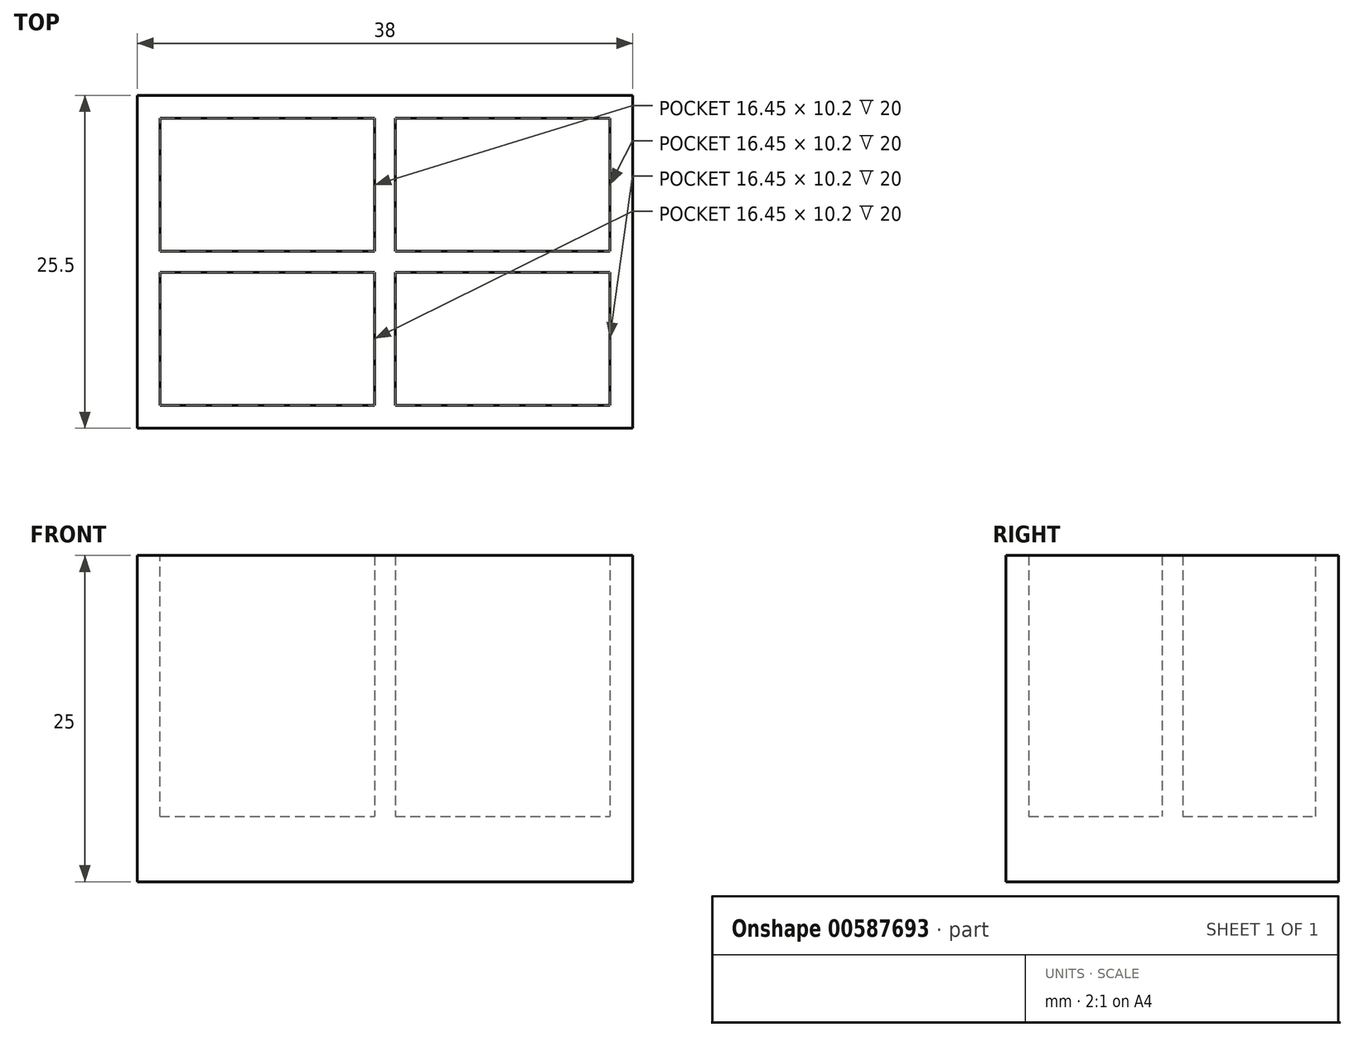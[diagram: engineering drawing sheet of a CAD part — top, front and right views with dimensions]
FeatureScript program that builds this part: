
annotation { "Feature Type Name" : "Feature", "Feature Type Description" : "" }
export const myFeature = defineFeature(function(context is Context, id is Id, definition is map)
    precondition{}
    {
        {
            var Q0;
            Q0=qCreatedBy(makeId("Top.planeOp"),FACE);
            var sketch = newSketch(context, id + "F0", { "sketchPlane" : qUnion([Q0])});
            skLineSegment(sketch, "E0.bottom", {"start": v(-19, -12.75) * mm, "end": v(19, -12.75) * mm});
            skLineSegment(sketch, "E0.top", {"start": v(-19, 12.75) * mm, "end": v(19, 12.75) * mm});
            skLineSegment(sketch, "E0.left", {"start": v(-19, -12.75) * mm, "end": v(-19, 12.75) * mm});
            skLineSegment(sketch, "E0.right", {"start": v(19, -12.75) * mm, "end": v(19, 12.75) * mm});
            skPoint(sketch, "E0.middle", {"position": v(0, 0) * mm});
            skSolve(sketch);
        }
        {
            var Q0;
            Q0=makeQuery(id+"F0.imprint","IMPRINT",FACE,{"disambiguationData":[TD([[makeQuery(id+"F0.imprint","IMPRINT",EDGE,{"derivedFrom":sQuery(id+"F0.wireOp",EDGE,"E0.bottom")}),1.0]])]});
            extrude(context, id + "F1", {"entities" : qUnion([Q0]), "depth" : 25 * mm, "offsetDistance" : 25 * mm});
        }
        {
            var Q0;
            Q0=makeQuery(id+"F1.opExtrude","CAP_FACE",FACE,{"disambiguationData":[OSD([sQuery(id+"F0.wireOp",EDGE,"E0.bottom"),sQuery(id+"F0.wireOp",EDGE,"E0.top"),sQuery(id+"F0.wireOp",EDGE,"E0.left"),sQuery(id+"F0.wireOp",EDGE,"E0.right")])],"isStart":false});
            var sketch = newSketch(context, id + "F2", { "sketchPlane" : qUnion([Q0])});
            skLineSegment(sketch, "E1.bottom", {"start": v(17.25, -11) * mm, "end": v(-17.25, -11) * mm});
            skLineSegment(sketch, "E1.top", {"start": v(17.25, 11) * mm, "end": v(-17.25, 11) * mm});
            skLineSegment(sketch, "E1.left", {"start": v(17.25, -11) * mm, "end": v(17.25, 11) * mm});
            skLineSegment(sketch, "E1.right", {"start": v(-17.25, -11) * mm, "end": v(-17.25, 11) * mm});
            skPoint(sketch, "E1.middle", {"position": v(0, 0) * mm});
            skSolve(sketch);
        }
        {
            var Q0;
            Q0=makeQuery(id+"F2.imprint","IMPRINT",FACE,{"disambiguationData":[TD([[makeQuery(id+"F2.imprint","IMPRINT",EDGE,{"derivedFrom":sQuery(id+"F2.wireOp",EDGE,"E1.bottom")}),-1.0]])]});
            extrude(context, id + "F3", {"entities" : qUnion([Q0]), "operationType" : NewBodyOperationType.REMOVE, "oppositeDirection" : true, "depth" : 20 * mm, "offsetDistance" : 25 * mm});
        }
        {
            var Q0;
            Q0=makeQuery(id+"F3.boolean.opBoolean","COPY",FACE,{"derivedFrom":makeQuery(id+"F3.opExtrude","CAP_FACE",FACE,{"disambiguationData":[OSD([sQuery(id+"F2.wireOp",EDGE,"E1.bottom"),sQuery(id+"F2.wireOp",EDGE,"E1.top"),sQuery(id+"F2.wireOp",EDGE,"E1.left"),sQuery(id+"F2.wireOp",EDGE,"E1.right")])],"isStart":false})});
            var sketch = newSketch(context, id + "F4", { "sketchPlane" : qUnion([Q0])});
            skLineSegment(sketch, "E2.bottom", {"start": v(0.8, -11) * mm, "end": v(-0.8, -11) * mm});
            skLineSegment(sketch, "E2.top", {"start": v(0.8, 11) * mm, "end": v(-0.8, 11) * mm});
            skLineSegment(sketch, "E2.left", {"start": v(0.8, -11) * mm, "end": v(0.8, 11) * mm});
            skLineSegment(sketch, "E2.right", {"start": v(-0.8, -11) * mm, "end": v(-0.8, 11) * mm});
            skPoint(sketch, "E2.middle", {"position": v(0, 0) * mm});
            skLineSegment(sketch, "E3.bottom", {"start": v(-17.25, -0.8) * mm, "end": v(17.25, -0.8) * mm});
            skLineSegment(sketch, "E3.top", {"start": v(-17.25, 0.8) * mm, "end": v(17.25, 0.8) * mm});
            skLineSegment(sketch, "E3.left", {"start": v(-17.25, -0.8) * mm, "end": v(-17.25, 0.8) * mm});
            skLineSegment(sketch, "E3.right", {"start": v(17.25, -0.8) * mm, "end": v(17.25, 0.8) * mm});
            skSolve(sketch);
        }
        {
            var Q0;
            {var subQ5=sQuery(id+"F4.wireOp",EDGE,"E3.left");Q0=makeQuery(id+"F4.imprint","IMPRINT",FACE,{"disambiguationData":[TD([[makeQuery(id+"F4.imprint","IMPRINT",EDGE,{"derivedFrom":subQ5}),-1.0]])]});}
            var Q1;
            {var subQ0=sQuery(id+"F4.wireOp",EDGE,"E2.bottom");Q1=makeQuery(id+"F4.imprint","IMPRINT",FACE,{"disambiguationData":[TD([[makeQuery(id+"F4.imprint","IMPRINT",EDGE,{"derivedFrom":subQ0}),-1.0]])]});}
            var Q2;
            {var subQ0=sQuery(id+"F4.wireOp",EDGE,"E3.bottom");var subQ1=sQuery(id+"F4.wireOp",EDGE,"E2.left");var subQ2=makeQuery(id+"F4.imprint","INTERSECT",VERTEX,{"derivedFrom":[subQ1,subQ0]});Q2=makeQuery(id+"F4.imprint","IMPRINT",FACE,{"disambiguationData":[TD([[makeQuery(id+"F4.imprint","IMPRINT",EDGE,{"disambiguationData":[TD([[subQ2,-1.0]])],"derivedFrom":subQ1}),1.0]])]});}
            var Q3;
            {var subQ0=sQuery(id+"F4.wireOp",EDGE,"E2.top");Q3=makeQuery(id+"F4.imprint","IMPRINT",FACE,{"disambiguationData":[TD([[makeQuery(id+"F4.imprint","IMPRINT",EDGE,{"derivedFrom":subQ0}),1.0]])]});}
            var Q4;
            {var subQ5=sQuery(id+"F4.wireOp",EDGE,"E3.right");Q4=makeQuery(id+"F4.imprint","IMPRINT",FACE,{"disambiguationData":[TD([[makeQuery(id+"F4.imprint","IMPRINT",EDGE,{"derivedFrom":subQ5}),1.0]])]});}
            extrude(context, id + "F5", {"entities" : qUnion([Q0, Q1, Q2, Q3, Q4]), "operationType" : NewBodyOperationType.ADD, "depth" : 20 * mm, "offsetDistance" : 25 * mm});
        }
    });
